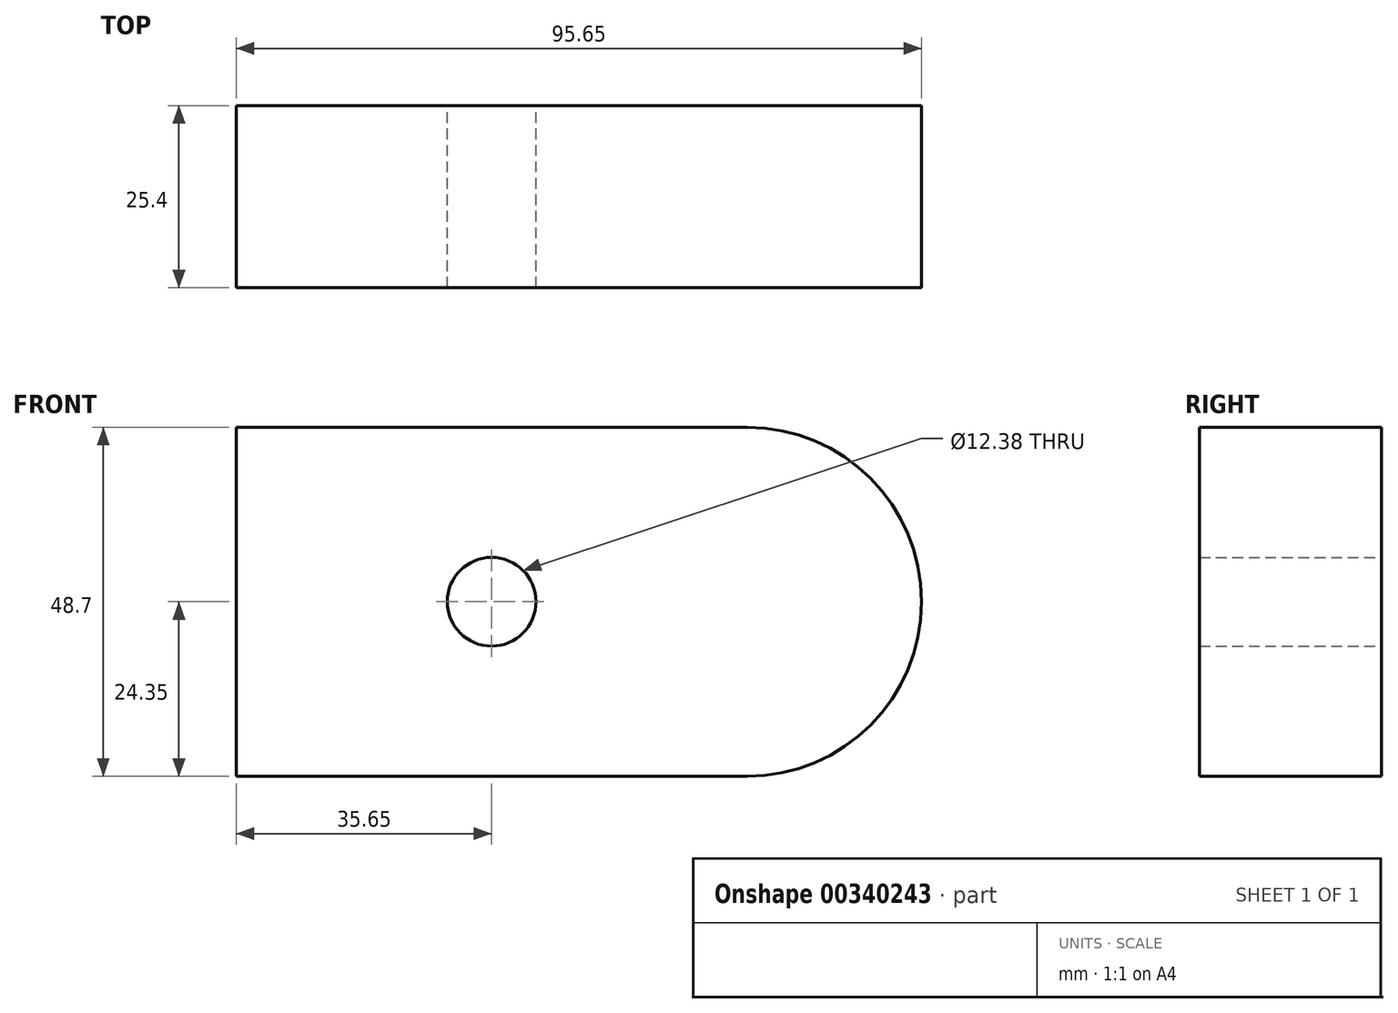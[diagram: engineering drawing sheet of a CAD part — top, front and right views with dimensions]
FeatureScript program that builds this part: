
annotation { "Feature Type Name" : "Feature", "Feature Type Description" : "" }
export const myFeature = defineFeature(function(context is Context, id is Id, definition is map)
    precondition{}
    {
        {
            var Q0;
            Q0=qCreatedBy(makeId("Front.planeOp"),FACE);
            var sketch = newSketch(context, id + "F0", { "sketchPlane" : qUnion([Q0])});
            skLineSegment(sketch, "E0.bottom", {"start": v(35.65, 24.35) * mm, "end": v(-35.65, 24.35) * mm});
            skLineSegment(sketch, "E0.top", {"start": v(35.65, -24.35) * mm, "end": v(-35.65, -24.35) * mm});
            skLineSegment(sketch, "E0.left", {"start": v(35.65, 24.35) * mm, "end": v(35.65, -24.35) * mm});
            skLineSegment(sketch, "E0.right", {"start": v(-35.65, 24.35) * mm, "end": v(-35.65, -24.35) * mm});
            skPoint(sketch, "E0.middle", {"position": v(0, 0) * mm});
            skCircle(sketch, "E1", {"center": v(35.65, 0) * mm, "radius": 24.35 * mm});
            skCircle(sketch, "E2", {"center": v(0, 0) * mm, "radius": 6.19 * mm});
            skSolve(sketch);
        }
        {
            var Q0;
            {var subQ2=sQuery(id+"F0.wireOp",EDGE,"E0.bottom");Q0=makeQuery(id+"F0.imprint","IMPRINT",FACE,{"disambiguationData":[TD([[makeQuery(id+"F0.imprint","IMPRINT",EDGE,{"derivedFrom":subQ2}),1.0]])]});}
            var Q1;
            {var subQ0=sQuery(id+"F0.wireOp",EDGE,"E0.left");Q1=makeQuery(id+"F0.imprint","IMPRINT",FACE,{"disambiguationData":[TD([[makeQuery(id+"F0.imprint","IMPRINT",EDGE,{"derivedFrom":subQ0}),-1.0]])]});}
            var Q2;
            {var subQ0=sQuery(id+"F0.wireOp",EDGE,"E0.left");Q2=makeQuery(id+"F0.imprint","IMPRINT",FACE,{"disambiguationData":[TD([[makeQuery(id+"F0.imprint","IMPRINT",EDGE,{"derivedFrom":subQ0}),1.0]])]});}
            extrude(context, id + "F1", {"entities" : qUnion([Q0, Q1, Q2]), "depth" : 25.4 * mm});
        }
    });
